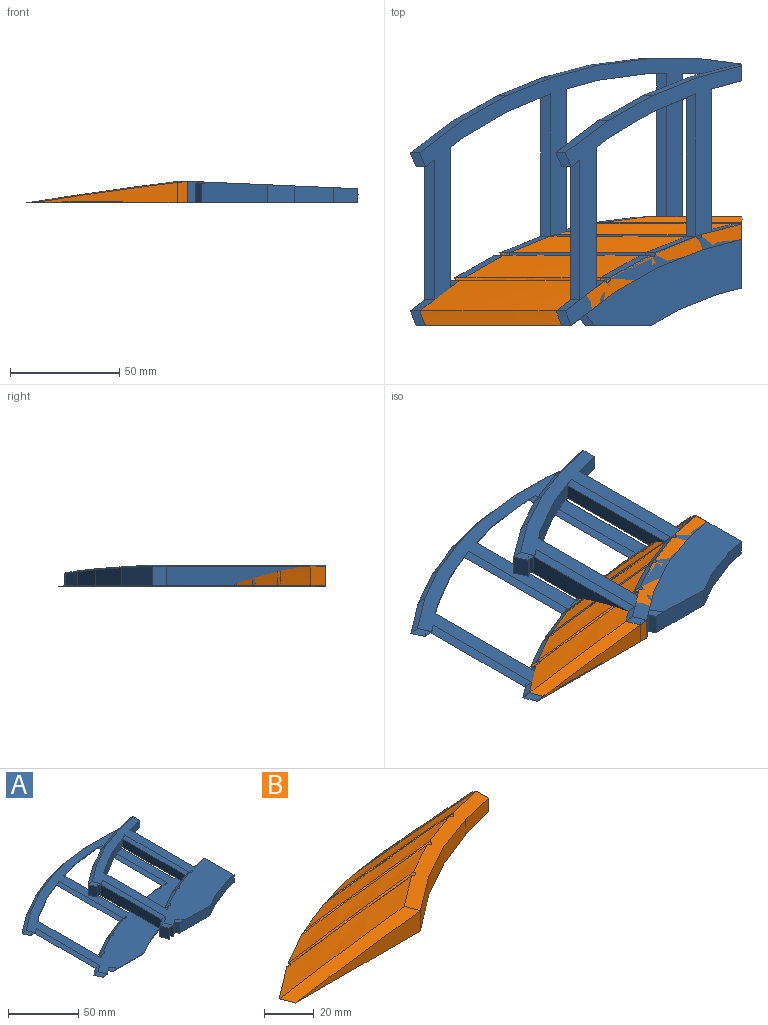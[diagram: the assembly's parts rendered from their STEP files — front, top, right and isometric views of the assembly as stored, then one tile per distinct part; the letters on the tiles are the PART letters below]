
ASSEMBLY  parts=2 mates=1
PART A: 148 faces, bbox 157.1x124.1x103.5 mm
  f0: plane 148.12x122.51mm, normal (0,0,1), area 3637.4mm2, adj f1,f90,f91,f92,f93,f94,f95,f96
  f1: plane 20.92x7.03mm, normal (-0.25,0.97,0), area 137.4mm2, adj f0,f2,f79,f90,f93,f123
  f2: revolved ~25.18x5.47mm, area 25.5mm2, adj f1,f3,f77,f78,f122
  f3: plane 119.2x81.38mm, normal (0.04,0,1), area 3593.7mm2, adj f2,f4,f5,f6,f8,f9,f15,f16
  f4: plane 17.9x7.79mm, normal (0.37,-0.93,0), area 142.6mm2, adj f3,f5,f39,f79
  f5: plane 12.57x8.33mm, normal (0.49,-0.87,0), area 116.2mm2, adj f3,f4,f6,f79
  f6: plane 30.33x9.47mm, normal (0,-1,0), area 271.4mm2, adj f3,f5,f7,f8,f79
  f7: plane 9.09x3.07mm, normal (-0.78,-0.63,0), area 35.6mm2, adj f6,f8,f9,f79
  f8: revolved ~8.37x5.09mm, area 17.7mm2, adj f3,f6,f7,f9
  f9: plane 9.94x6.65mm, normal (0.61,-0.79,0), area 50.9mm2, adj f3,f7,f8,f10,f79
  f10: plane 9.94x2.51mm, normal (-0.93,-0.37,0), area 26mm2, adj f9,f11,f14,f79
  f11: plane 9.43x3.28mm, normal (0.61,-0.79,0), area 38.7mm2, adj f10,f12,f14,f79
  f12: plane 9.54x6.64mm, normal (-0.93,-0.37,0), area 67.7mm2, adj f11,f13,f15,f79
  f13: plane 9.54x6.65mm, normal (-0.61,0.8,0), area 78.6mm2, adj f12,f16,f79,f104
  f14: revolved ~7.55x2.51mm, area 5.5mm2, adj f10,f11,f15
  f15: revolved ~6.89x6.64mm, area 28.6mm2, adj f3,f12,f14,f16
  f16: revolved ~10.92x5.06mm, area 22.2mm2, adj f3,f13,f15,f17
  f17: cylinder r=1642.27mm len=64.03mm, axis (0,-1,0), area 268.2mm2, adj f3,f16,f18,f20,f104
  f18: plane 9.94x2.49mm, normal (-0.91,-0.4,0), area 20.3mm2, adj f17,f19,f20,f79,f101,f104
  f19: revolved ~7.44x2.49mm, area 5.5mm2, adj f18,f21,f101
  f20: plane 4.01x3.15mm, normal (0.62,-0.79,0), area 1.6mm2, adj f3,f17,f18
  f21: revolved ~7.12x6.44mm, area 27.8mm2, adj f3,f19,f22,f100
  f22: revolved ~23.65x14.62mm, area 64.2mm2, adj f3,f21,f23,f99
  f23: revolved ~24.87x11.57mm, area 51.3mm2, adj f3,f22,f24,f78
  f24: plane 20.6x11.57mm, normal (-0.49,0.87,0), area 196.8mm2, adj f23,f79,f93,f99
  f25: plane 13.8x7.13mm, normal (0.26,-0.96,0), area 97.6mm2, adj f3,f26,f79,f122
  f26: plane 65.44x7.13mm, normal (1,0,0), area 457.1mm2, adj f3,f25,f27,f35,f36,f37,f79
  f27: plane 10.62x6.3mm, normal (-0.25,0.97,0), area 66.6mm2, adj f26,f28,f36,f37
  f28: bspline ~92.21x2.73mm, area 7.3mm2, adj f27,f29,f30,f36
  f29: revolved ~3.97x0.89mm, area 2mm2, adj f28,f30,f37,f38
  f30: plane 6.28x2.57mm, normal (-0.25,0.97,0), area 7.6mm2, adj f28,f29,f31,f34,f36,f38
  f31: bspline ~92.21x2.73mm, area 6.4mm2, adj f30,f32,f34,f36
  f32: plane 5.78x0.87mm, normal (-0.13,0.99,0), area 5.1mm2, adj f31,f33,f36,f38
  f33: revolved ~1.74x0.11mm, area 0.1mm2, adj f32,f34,f38
  f34: revolved ~1.29x1.02mm, area 0.8mm2, adj f30,f31,f33,f38
  f35: plane 13.8x1.74mm, normal (0.13,0.99,0), area 4.5mm2, adj f26,f36,f38,f79
  f36: plane 14x5.26mm, normal (0,0,1), area 35.6mm2, adj f26,f27,f28,f30,f31,f32,f35,f38
  f37: revolved ~19.15x3.84mm, area 15.3mm2, adj f3,f26,f27,f29,f38
  f38: plane 30.31x6.64mm, normal (1,0,0), area 196.4mm2, adj f3,f29,f30,f32,f33,f34,f35,f36
  f39: plane 11x7mm, normal (0.25,-0.97,0), area 76.8mm2, adj f3,f4,f38,f79
  f40: revolved ~3.84x1.74mm, area 2.5mm2, adj f3,f41,f42
  f41: plane 2.65x0.96mm, normal (0.31,-0.95,0), area 0.4mm2, adj f3,f40,f42
  f42: bspline ~92.25x3.33mm, area 0.2mm2, adj f3,f40,f41
  f43: plane 64.35x9.57mm, normal (1,0,0), area 568.3mm2, adj f3,f44,f46,f47,f48,f61,f62,f63
  f44: plane 1.3x0.41mm, normal (-0.25,0.97,0), area 0.3mm2, adj f43,f45,f46,f63
  f45: bspline ~92.11x2.73mm, area 0.3mm2, adj f44,f48,f63
  f46: revolved ~1.5x0.33mm, area 0.2mm2, adj f43,f44,f47
  f47: revolved ~2.54x0.33mm, area 0.2mm2, adj f43,f46,f48
  f48: plane 84.18x41.85mm, normal (0,0,1), area 1102.7mm2, adj f43,f45,f47,f49,f50,f51,f52,f55
  f49: plane 18.73x7.51mm, normal (-0.37,0.93,0), area 142.8mm2, adj f48,f50,f60,f72
  f50: bspline ~92.25x3.52mm, area 31.1mm2, adj f48,f49,f51,f71
  f51: plane 18.29x10.28mm, normal (-0.49,0.87,0), area 165.4mm2, adj f48,f50,f61,f68
  f52: bspline ~92.11x2.44mm, area 0.2mm2, adj f48,f53,f55
  f53: plane 4.1x0.53mm, normal (-0.13,0.99,0), area 0.7mm2, adj f52,f54,f55,f79
  f54: revolved ~4.41x0.52mm, area 1.1mm2, adj f53,f62,f79
  f55: revolved ~5.4x1.22mm, area 2.8mm2, adj f48,f52,f53,f56,f79
  f56: plane 10.54x0.41mm, normal (0,1,0), area 2.6mm2, adj f48,f55,f57,f79
  f57: cylinder r=1628.88mm len=50.61mm, axis (0,-1,0), area 212mm2, adj f48,f56,f74,f79
  f58: plane 53.71x0.38mm, normal (1,0,0), area 20.2mm2, adj f48,f59,f74,f79
  f59: plane 1.92x0.38mm, normal (0,1,0), area 0.7mm2, adj f48,f58,f60,f79
  f60: plane 63.54x7.09mm, normal (-1,0,0), area 447.1mm2, adj f48,f49,f59,f73,f74,f79
  f61: bspline ~92.25x3.66mm, area 31.3mm2, adj f43,f48,f51,f67
  f62: revolved ~24.15x2.51mm, area 13.9mm2, adj f43,f48,f54,f63,f79
  f63: revolved ~4.74x1.39mm, area 3.2mm2, adj f43,f44,f45,f48,f62
  f64: revolved ~8.03x3.05mm, area 6.3mm2, adj f3,f43,f67
  f65: bspline ~92.26x3.66mm, area 0.2mm2, adj f3,f66,f67
  f66: plane 0.79x0.6mm, normal (-0.61,0.8,0), area 0.2mm2, adj f65,f67
  f67: revolved ~6.71x2.06mm, area 10.7mm2, adj f3,f43,f61,f64,f65,f66,f68
  f68: revolved ~22.56x10.28mm, area 45.6mm2, adj f3,f51,f67,f71
  f69: bspline ~92.26x3.52mm, area 0.2mm2, adj f3,f70,f71
  f70: plane 1.34x0.75mm, normal (-0.49,0.87,0), area 0.4mm2, adj f69,f71
  f71: revolved ~9.36x1.89mm, area 3.4mm2, adj f3,f50,f68,f69,f70,f72
  f72: revolved ~23x7.51mm, area 33.9mm2, adj f3,f49,f71,f73
  f73: cylinder r=1634.73mm len=65.33mm, axis (0,-1,0), area 275.7mm2, adj f3,f60,f72,f74
  f74: plane 19.93x8.35mm, normal (0.39,-0.92,0), area 132.7mm2, adj f3,f48,f57,f58,f60,f73,f75,f79
  f75: plane 20.6x12.18mm, normal (0.51,-0.86,0), area 209.9mm2, adj f3,f74,f76,f79
  f76: plane 9.44x5.13mm, normal (0.62,-0.79,0), area 60.8mm2, adj f3,f43,f75,f79
  f77: revolved ~6.34x0.41mm, area 0.9mm2, adj f2,f122,f123
  f78: revolved ~25.56x8.53mm, area 38.5mm2, adj f2,f3,f23,f93
  f79: plane 153.92x124.06mm, normal (0,0,-1), area 10433.6mm2, adj f1,f4,f5,f6,f7,f9,f10,f11
  f80: revolved ~8.51x0.41mm, area 0.9mm2, adj f79,f119,f120
  f81: revolved ~7.4x2.47mm, area 5.4mm2, adj f79,f82,f114
  f82: plane 2.47x1.09mm, normal (-0.91,-0.4,0), area 0.9mm2, adj f79,f81,f112,f113
  f83: revolved ~7.51x2.49mm, area 5.5mm2, adj f79,f84,f110
  f84: plane 2.49x0.98mm, normal (-0.93,-0.37,0), area 0.9mm2, adj f79,f83,f109
  f85: revolved ~4.75x0.99mm, area 1mm2, adj f79,f127,f140
  f86: revolved ~6.74x1.74mm, area 4.7mm2, adj f79,f87,f88,f89
  f87: plane 2.19x0.89mm, normal (-0.37,0.93,0), area 0.6mm2, adj f86,f88
  f88: plane 0.89x0.35mm, normal (-1,0,0), area 0.1mm2, adj f86,f87,f89
  f89: revolved ~6.66x0.83mm, area 2.6mm2, adj f79,f86,f88
  f90: revolved ~7.91x0.49mm, area 1.5mm2, adj f0,f1,f79,f91
  f91: plane 8.5x0.39mm, normal (0,-1,0), area 2.3mm2, adj f0,f79,f90,f92
  f92: plane 3.03x0.38mm, normal (1,0,0), area 1.1mm2, adj f0,f79,f91,f93
  f93: plane 21.3x8.53mm, normal (-0.37,0.93,0), area 167.4mm2, adj f0,f1,f24,f78,f79,f92,f94
  f94: cylinder r=1628.88mm len=7.73mm, axis (0,-1,0), area 29.3mm2, adj f0,f79,f93,f95
  f95: plane 7.45x0.42mm, normal (0,-1,0), area 2.2mm2, adj f0,f79,f94,f96
  f96: plane 23.36x3.14mm, normal (0.13,-0.99,0), area 10.5mm2, adj f0,f79,f95,f97
  f97: plane 14.9x4.06mm, normal (0.26,-0.96,0), area 7.6mm2, adj f0,f79,f96,f98
  f98: plane 25.59x0.51mm, normal (1,0,0), area 13.2mm2, adj f0,f79,f97,f99
  f99: plane 19.38x14.62mm, normal (-0.6,0.8,0), area 219mm2, adj f0,f22,f24,f79,f98,f100
  f100: plane 9.03x6.44mm, normal (-0.91,-0.4,0), area 63.1mm2, adj f0,f21,f99,f101
  f101: plane 9.43x3.17mm, normal (0.62,-0.79,0), area 36.4mm2, adj f0,f18,f19,f79,f100,f102
  f102: plane 31.33x0.52mm, normal (1,0,0), area 15.8mm2, adj f0,f79,f101,f103
  f103: revolved ~10.46x1.6mm, area 2.4mm2, adj f0,f79,f102,f104
  f104: plane 61.47x9.27mm, normal (-1,0,0), area 554.3mm2, adj f0,f13,f17,f18,f79,f103,f105
  f105: plane 17.08x6.84mm, normal (0.37,-0.93,0), area 9.8mm2, adj f0,f79,f104,f106
  f106: plane 12.58x7.07mm, normal (0.49,-0.87,0), area 8.2mm2, adj f0,f79,f105,f107
  f107: plane 30.33x0.66mm, normal (0,-1,0), area 17.6mm2, adj f0,f79,f106,f108
  f108: revolved ~8.35x5.09mm, area 17.7mm2, adj f0,f79,f107,f109
  f109: plane 6.66x5.09mm, normal (0.61,-0.79,0), area 4.6mm2, adj f0,f79,f84,f108
  f110: revolved ~6.87x6.64mm, area 28.6mm2, adj f0,f79,f83,f111
  f111: revolved ~10.91x5.06mm, area 22.2mm2, adj f0,f79,f110,f112
  f112: cylinder r=1642.27mm len=64.03mm, axis (0,-1,0), area 268.2mm2, adj f0,f79,f82,f111,f113
  f113: plane 4.02x3.15mm, normal (0.62,-0.79,0), area 1.6mm2, adj f0,f82,f112
  f114: revolved ~7.09x6.44mm, area 27.8mm2, adj f0,f79,f81,f115
  f115: revolved ~23.64x14.62mm, area 64.2mm2, adj f0,f79,f114,f116
  f116: revolved ~24.87x11.57mm, area 51.3mm2, adj f0,f79,f115,f117
  f117: revolved ~25.56x8.53mm, area 38.5mm2, adj f0,f79,f116,f118
  f118: revolved ~25.18x5.47mm, area 25.7mm2, adj f0,f79,f117,f119
  f119: revolved ~27.6x3.02mm, area 16.7mm2, adj f0,f79,f80,f118
  f120: plane 23.46x0.44mm, normal (0,1,0), area 9mm2, adj f0,f79,f80,f121
  f121: plane 18.78x2.43mm, normal (0.13,0.99,0), area 6.2mm2, adj f0,f79,f120,f122
  f122: plane 7.67x6.52mm, normal (1,0,0), area 49.2mm2, adj f0,f2,f3,f25,f77,f79,f121,f123
  f123: plane 5.87x3.17mm, normal (-0.13,0.99,0), area 18.6mm2, adj f0,f1,f77,f122
  f124: bspline ~92.11x3.33mm, area 0.2mm2, adj f0,f125,f126
  f125: revolved ~3.85x1.74mm, area 2.6mm2, adj f0,f124,f126
  f126: plane 2.65x0.96mm, normal (0.31,-0.95,0), area 0.4mm2, adj f0,f124,f125
  f127: revolved ~8.04x3.05mm, area 6.3mm2, adj f0,f85,f130,f140
  f128: bspline ~92.11x3.67mm, area 0.2mm2, adj f0,f129,f130
  f129: plane 0.79x0.6mm, normal (-0.6,0.8,0), area 0.2mm2, adj f128,f130
  f130: revolved ~9x2.66mm, area 6.9mm2, adj f0,f79,f127,f128,f129,f131
  f131: revolved ~22.55x10.28mm, area 45.6mm2, adj f0,f79,f130,f134
  f132: bspline ~92.11x3.52mm, area 0.2mm2, adj f0,f133,f134
  f133: plane 1.34x0.75mm, normal (-0.49,0.87,0), area 0.4mm2, adj f132,f134
  f134: revolved ~9.33x1.89mm, area 3.4mm2, adj f0,f79,f131,f132,f133,f135
  f135: revolved ~23x7.51mm, area 33.9mm2, adj f0,f79,f134,f136
  f136: cylinder r=1634.73mm len=65.33mm, axis (0,-1,0), area 275.8mm2, adj f0,f79,f135,f137
  f137: plane 19.95x8.35mm, normal (0.39,-0.92,0), area 10.9mm2, adj f0,f79,f136,f138
  f138: plane 20.62x12.18mm, normal (0.51,-0.86,0), area 14.7mm2, adj f0,f79,f137,f139
  f139: plane 5.13x4.02mm, normal (0.62,-0.79,0), area 4.2mm2, adj f0,f79,f138,f140
  f140: plane 64.24x0.68mm, normal (1,0,0), area 40.9mm2, adj f0,f79,f85,f127,f139
  f141: plane 2.19x0.89mm, normal (-0.37,0.93,0), area 0.5mm2, adj f142,f143
  f142: plane 0.89x0.35mm, normal (-1,0,0), area 0.1mm2, adj f141,f143,f144
  f143: revolved ~6.75x1.74mm, area 4.7mm2, adj f141,f142,f144,f146
  f144: revolved ~6.68x0.83mm, area 2.6mm2, adj f142,f143,f145
  f145: plane 6.72x2.52mm, normal (0.31,-0.95,0), area 17.7mm2, adj f144,f146,f147
  f146: bspline ~92.24x3.33mm, area 27.7mm2, adj f143,f145,f147
  f147: plane 2.96x2.11mm, normal (0,0,1), area 2.8mm2, adj f145,f146
PART B: 33 faces, bbox 172.6x50.6x95.5 mm
  f0: plane 11.16x7.29mm, normal (1,0,0), area 60.3mm2, adj f18,f19,f20,f21,f22,f23,f24,f25
  f1: plane 2.27x0.91mm, normal (-0.37,0.93,0), area 0.7mm2, adj f6,f7
  f2: plane 1.34x0.75mm, normal (-0.49,0.87,0), area 0.4mm2, adj f5,f9
  f3: plane 1.43x1.24mm, normal (-0.61,0.8,0), area 0.2mm2, adj f4,f11
  f4: bspline ~92.26x3.66mm, area 0.2mm2, adj f3,f11,f32
  f5: bspline ~92.26x3.52mm, area 0.2mm2, adj f2,f9,f32
  f6: bspline ~92.25x3.33mm, area 0.2mm2, adj f1,f7,f32
  f7: revolved ~73.52x7.44mm, area 190mm2, adj f1,f6,f8,f18,f28,f32
  f8: revolved ~89.79x8.27mm, area 567.4mm2, adj f7,f9,f18,f32
  f9: revolved ~73.47x8.37mm, area 192.4mm2, adj f2,f5,f8,f10,f18,f32
  f10: revolved ~89.26x10.28mm, area 759.3mm2, adj f9,f11,f18,f32
  f11: revolved ~73.41x9.27mm, area 194.9mm2, adj f3,f4,f10,f12,f18,f32
  f12: revolved ~89.05x13.73mm, area 1004.3mm2, adj f11,f13,f18,f32
  f13: revolved ~73.61x10.06mm, area 476.9mm2, adj f12,f14,f18,f32
  f14: plane 70.99x9.94mm, normal (0,-1,0), area 371.5mm2, adj f13,f15,f18
  f15: plane 20.22x15.47mm, normal (0.61,-0.79,0), area 241.9mm2, adj f14,f16,f18,f32
  f16: plane 19.82x11.15mm, normal (0.49,-0.87,0), area 196.2mm2, adj f15,f17,f18,f32
  f17: plane 20.53x8.19mm, normal (0.37,-0.93,0), area 170.9mm2, adj f16,f18,f31,f32
  f18: plane 151.88x49.78mm, normal (0,0,-1), area 4053.4mm2, adj f0,f7,f8,f9,f10,f11,f12,f13
  f19: plane 2.53x0.79mm, normal (-0.25,0.97,0), area 0.2mm2, adj f0,f18,f23,f24
  f20: revolved ~42.93x2.51mm, area 38.9mm2, adj f0,f18,f21,f24
  f21: revolved ~27.63x1.98mm, area 56.4mm2, adj f0,f18,f20,f29
  f22: revolved ~1.64x0.21mm, area 0.1mm2, adj f0,f18,f23
  f23: revolved ~1.2x0.57mm, area 0.4mm2, adj f0,f18,f19,f22
  f24: revolved ~3.92x1.32mm, area 3.3mm2, adj f0,f18,f19,f20
  f25: revolved ~49.91x4.04mm, area 108.7mm2, adj f0,f18,f26,f29
  f26: revolved ~87.41x6.14mm, area 189.2mm2, adj f0,f18,f25,f27
  f27: revolved ~72.14x6.4mm, area 161.6mm2, adj f0,f18,f26,f28,f30
  f28: revolved ~90.58x7.33mm, area 397.1mm2, adj f0,f7,f18,f27,f32
  f29: plane 45.31x3.81mm, normal (0,1,0), area 65.4mm2, adj f0,f18,f21,f25
  f30: plane 2.6x0.68mm, normal (-0.25,0.97,0), area 0.6mm2, adj f0,f27
  f31: plane 17.7x7.3mm, normal (0.25,-0.97,0), area 126.5mm2, adj f0,f17,f18,f32
  f32: plane 81.17x46.69mm, normal (0.04,0,1), area 605mm2, adj f0,f4,f5,f6,f7,f8,f9,f10
PLACE A t=(-20.14,3.27,11.85)mm
PLACE B t=(-20.14,3.27,11.85)mm
MATE fastened A.f79 <-> B.f18  axis (0,0,-1) through (89.96,-264.31,200.2)mm
